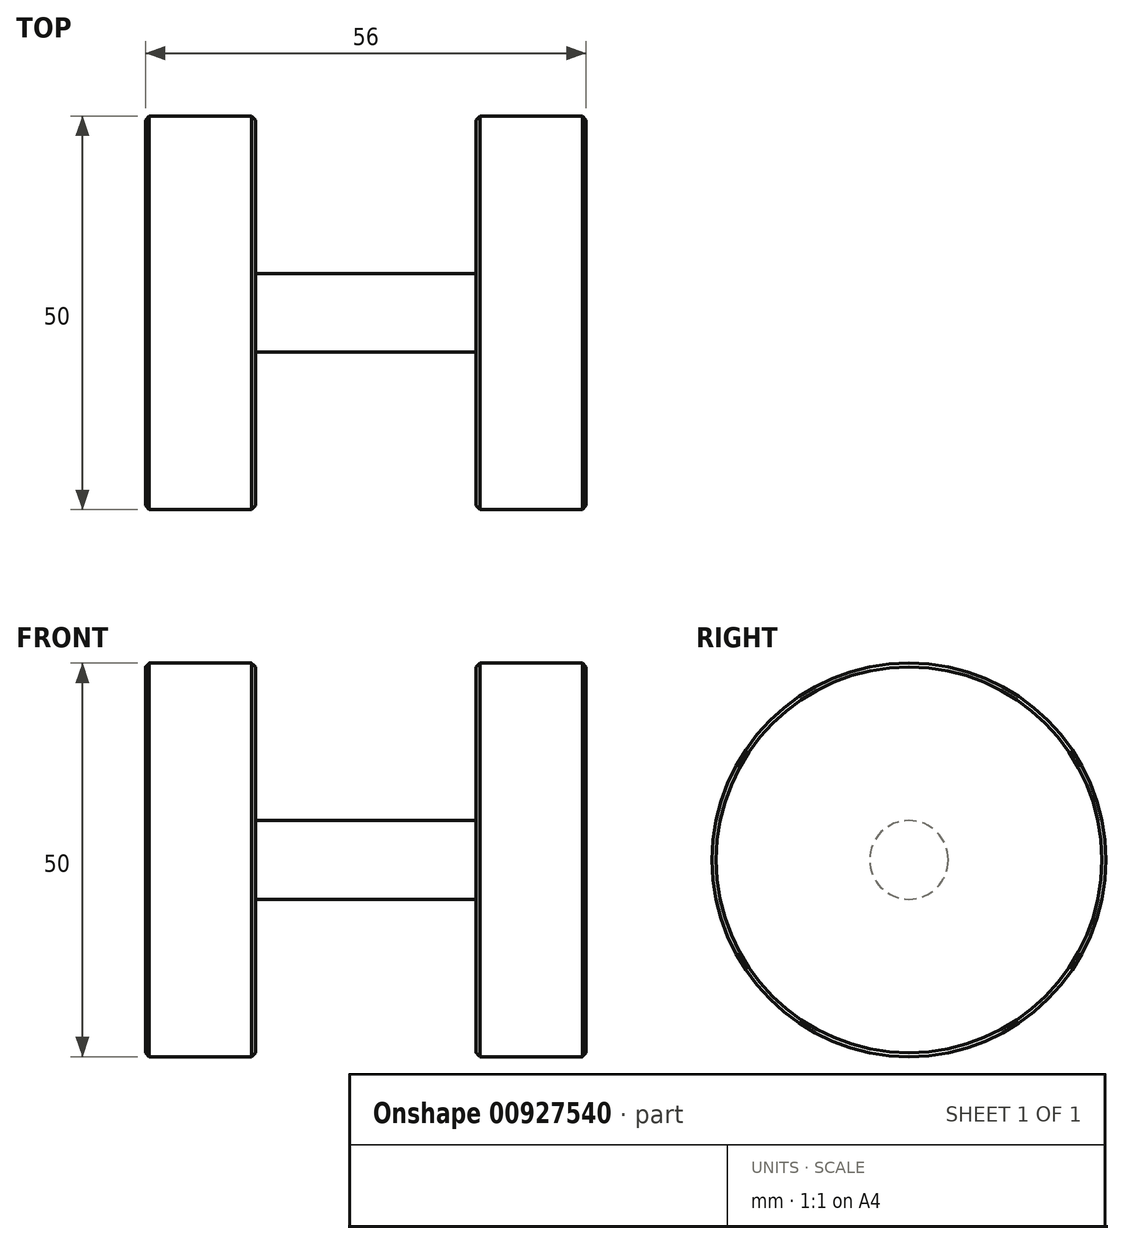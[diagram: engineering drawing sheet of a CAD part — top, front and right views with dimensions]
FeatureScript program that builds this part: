
annotation { "Feature Type Name" : "Feature", "Feature Type Description" : "" }
export const myFeature = defineFeature(function(context is Context, id is Id, definition is map)
    precondition{}
    {
        {
            var Q0;
            Q0=qCreatedBy(makeId("Right.planeOp"),FACE);
            var sketch = newSketch(context, id + "F0", { "sketchPlane" : qUnion([Q0])});
            skCircle(sketch, "E0", {"center": v(0, 0) * mm, "radius": 25 * mm});
            skSolve(sketch);
        }
        {
            var Q0;
            Q0 = qSketchRegion(id + "F0", true);
            extrude(context, id + "F1", {"entities" : qUnion([Q0]), "depth" : 14 * mm, "offsetDistance" : 25 * mm});
        }
        {
            var Q0;
            Q0=makeQuery(id+"F1.opExtrude","CAP_FACE",FACE,{"disambiguationData":[OSD([sQuery(id+"F0.wireOp",EDGE,"E0")])],"isStart":true});
            var sketch = newSketch(context, id + "F2", { "sketchPlane" : qUnion([Q0])});
            skCircle(sketch, "E1", {"center": v(0, 0) * mm, "radius": 5 * mm});
            skSolve(sketch);
        }
        {
            var Q0;
            Q0 = qSketchRegion(id + "F2", true);
            extrude(context, id + "F3", {"entities" : qUnion([Q0]), "operationType" : NewBodyOperationType.ADD, "depth" : 28 * mm, "offsetDistance" : 25 * mm});
        }
        {
            var Q0;
            Q0=makeQuery(id+"F3.opExtrude","CAP_FACE",FACE,{"disambiguationData":[OSD([sQuery(id+"F2.wireOp",EDGE,"E1")])],"isStart":false});
            var sketch = newSketch(context, id + "F4", { "sketchPlane" : qUnion([Q0])});
            skCircle(sketch, "E2", {"center": v(0, 0) * mm, "radius": 25 * mm});
            skSolve(sketch);
        }
        {
            var Q0;
            Q0 = qSketchRegion(id + "F4", true);
            extrude(context, id + "F5", {"entities" : qUnion([Q0]), "operationType" : NewBodyOperationType.ADD, "depth" : 14 * mm, "offsetDistance" : 25 * mm});
        }
        {
            var Q0;
            Q0=makeQuery(id+"F1.opExtrude","CAP_EDGE",EDGE,{"disambiguationData":[OSD([sQuery(id+"F0.wireOp",EDGE,"E0")])],"isStart":false});
            var Q1;
            Q1=makeQuery(id+"F1.opExtrude","CAP_EDGE",EDGE,{"disambiguationData":[OSD([sQuery(id+"F0.wireOp",EDGE,"E0")])],"isStart":true});
            var Q2;
            Q2=makeQuery(id+"F5.opExtrude","SWEPT_FACE",FACE,{"disambiguationData":[OSD([sQuery(id+"F4.wireOp",EDGE,"E2")])]});
            chamfer(context, id + "F6", {"entities" : qUnion([Q0, Q1, Q2]), "width" : 0.5 * mm, "tangentPropagation" : true});
        }
    });
